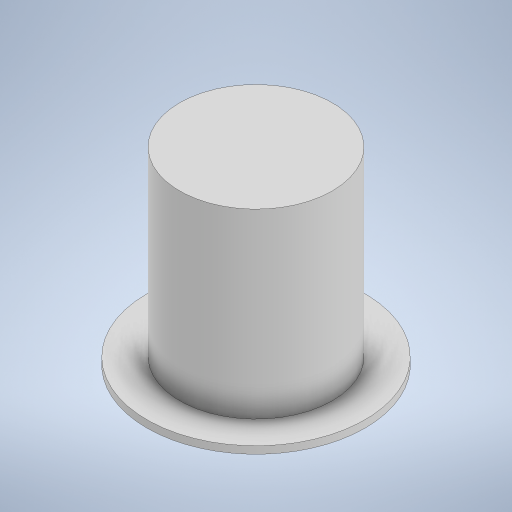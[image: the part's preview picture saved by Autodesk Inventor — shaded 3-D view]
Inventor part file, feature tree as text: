
AUTODESK INVENTOR PART (.ipt)
format: ipt  version: 2024.1 (Build 281209000, 209)  size: 223,744 bytes
history: native  units: mm
features: extrude x2, sketch x2, other x1
ambient origin geometry x8: Origin, YZ Plane, XZ Plane, XY Plane, X Axis, Y Axis, Z Axis, Center Point
bodies: Body1 (feature_tree)
feature tree (5):
  other  "ソリッド1"
  extrude  "押し出し1"  Depth=30.0mm
  extrude  "押し出し2"  Depth=1.0mm TaperAngle=0.0deg
  sketch  "スケッチ1"
  sketch  "スケッチ2"
